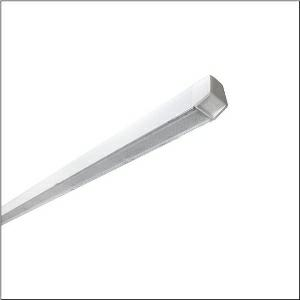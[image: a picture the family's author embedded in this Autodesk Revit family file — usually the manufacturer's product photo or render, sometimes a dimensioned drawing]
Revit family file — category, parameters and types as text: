
# Revit family: licross_r__11_recessed_mo_51ul1edv4e5f00s_da31
name_source: partatom
category: Lighting Fixtures
units: mm (PartAtom-declared; Revit-internal decimal feet)

## family parameters
Cut with Voids When Loaded = No
Host = Face
Light Source = No
Part Type = Normal
Room Calculation Point = No
Round Connector Dimension = Use Diameter
Shared = No

## types (1)
- --- (1 x LED, 14910 lm, 89.6 W, 4000K)
    Apparent Load = 90 VA
    CIE Flux Codes = 85 95 99 100 100
    Color Rendering = 80
    Color Temperature = 4000K
    Default Elevation = 1800 mm
    Description = Licross® 11 Recessed MO, single luminaire, primary optical cover: cover, of PMMA, light emission: direct distribution, primary light characteristic: symmetric, installation type: slip-in mounting, LED, rated luminous flux: 14.910lm, luminous efficacy: 166lm/W, light colour: 840, colour temperature: 4000K, control gear: ECG DALI, with terminal, 5-pole, max. 2.5mm², mains connection: 230V, AC, 50/60Hz, rated input power: 90W, Licross® LED insert, of sheet steel, galvanised, coil coated, white, length: 2.327mm, width: 70mm, height: 71mm, end cap, of PC, white, mounting rail, of sheet steel, galvanised, white, protection rating (complete): IP20, insulation class (complete): insulation class I (protective earthing), certification: CE, ENEC, VDE, UKCA, impact resistance: IK06, permissible operating ambient temperature: -25..+35°C, corresponds to IFS (International Featured Standards) requirements for safety and quality in the food industry, reducing of maximum allowable ambient temperature of 5°C with ceiling mounting, LABS conformity tested according to VDMA 24364:2018-05, packaging unit: 1 piece
    Height = 58 mm
    Lamp = 1 x LED
    Lamp Light Flux = 14910 lm
    Lamp Power = 89.6 W
    Lamp count = 1
    Length = 2250 mm
    Luminous efficacy = 166 lm/W
    Manufacturer = Siteco
    ModVariant = No
    Model = 51UL1EDV4E5F00S
    Mounting Place = Ceiling
    Mounting Type = Pendant
    Number of Poles = 1
    OnlyDefault = Yes
    Power Factor = 1
    Product Name = Licross® 11 Recessed MO
    Product group = single luminaire
    ProductGroupID = 909
    Protection Class = Protection class I
    Protection Degree = IP 20
    RLX_Detail_Level = 1
    RlxData = <blob elided: 32033 chars, md5=2ed9e8eb>
    Socket = socket
    Standby Power = 0 W
    System Light Flux = 14910 lm
    System Power = 90 W
    Type Comments = factory setting: luminous flux: 100 % | dim-lin: 254 | 400 mA
    Type Image = l_1006979.jpg
    URL = http://relux.com
    VarID = @adj_092629
    Voltage = 0 V
    Weight = 0.00 kg
    Width = 66 mm

## geometry (parser evidence)
native form markers: Blend x4, Sweep x11
no freeform markers — native parametric forms only
